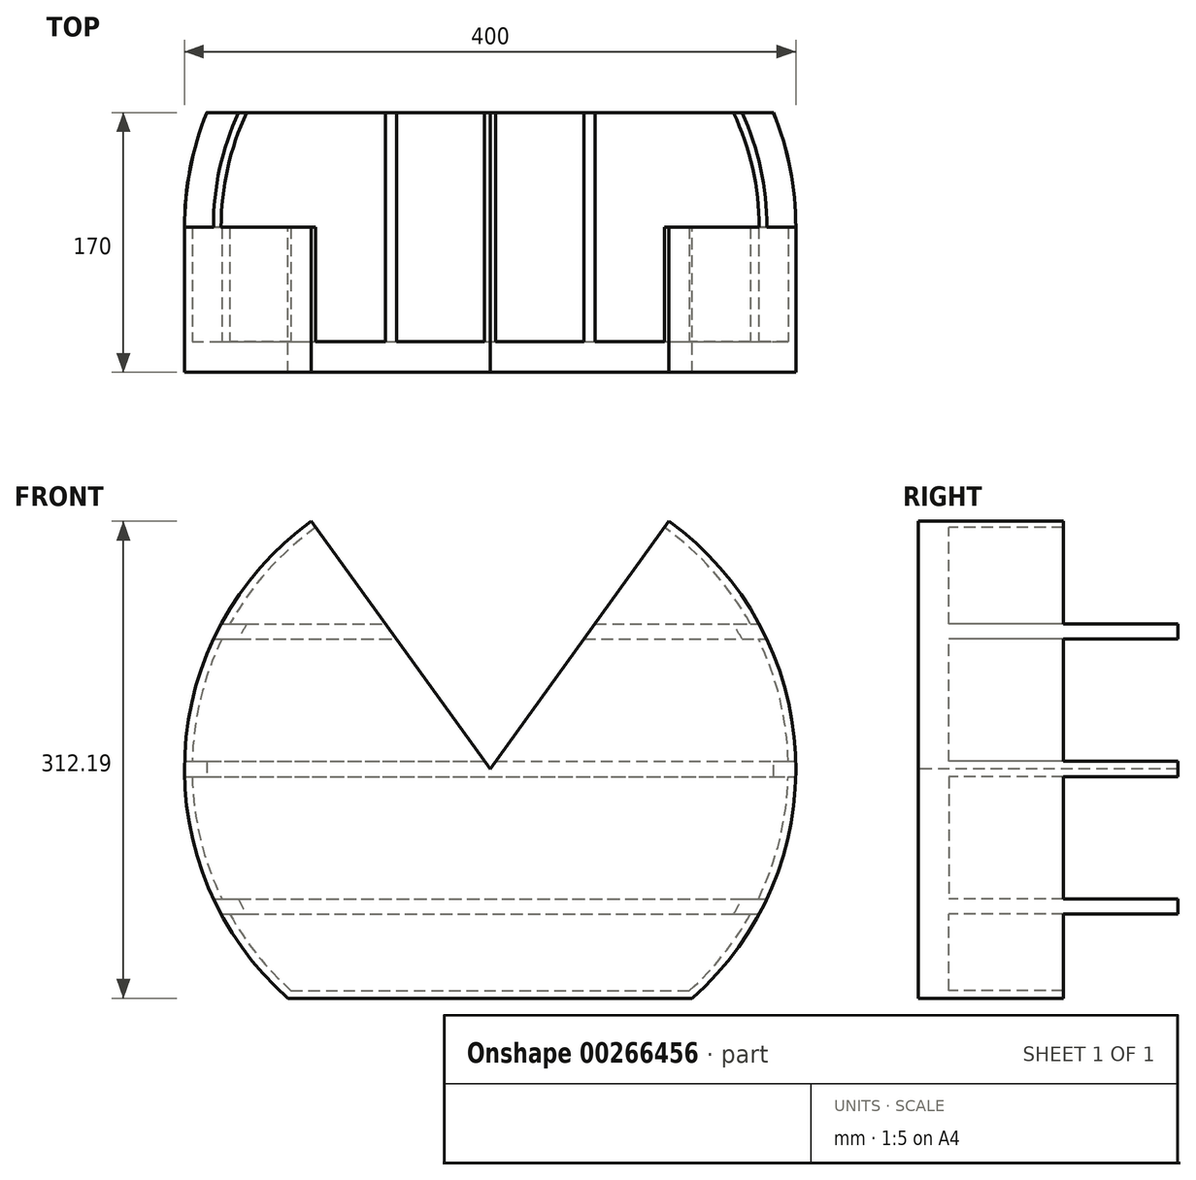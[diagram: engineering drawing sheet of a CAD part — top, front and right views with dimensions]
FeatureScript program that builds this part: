
annotation { "Feature Type Name" : "Feature", "Feature Type Description" : "" }
export const myFeature = defineFeature(function(context is Context, id is Id, definition is map)
    precondition{}
    {
        {
            var Q0;
            Q0=qCreatedBy(makeId("Front.planeOp"),FACE);
            var sketch = newSketch(context, id + "F0", { "sketchPlane" : qUnion([Q0])});
            skCircle(sketch, "E0", {"center": v(0, 0) * mm, "radius": 200 * mm});
            skSolve(sketch);
        }
        {
            var Q0;
            Q0=makeQuery(id+"F0.imprint","IMPRINT",FACE,{"disambiguationData":[TD([[makeQuery(id+"F0.imprint","IMPRINT",EDGE,{"derivedFrom":sQuery(id+"F0.wireOp",EDGE,"E0")}),1.0]])]});
            extrude(context, id + "F1", {"entities" : qUnion([Q0]), "depth" : 20 * mm});
        }
        {
            var Q0;
            Q0=makeQuery(id+"F1.opExtrude","CAP_FACE",FACE,{"disambiguationData":[OSD([sQuery(id+"F0.wireOp",EDGE,"E0")])],"isStart":true});
            var sketch = newSketch(context, id + "F2", { "sketchPlane" : qUnion([Q0])});
            skLineSegment(sketch, "E1.bottom", {"start": v(225, 5) * mm, "end": v(-225, 5) * mm});
            skLineSegment(sketch, "E1.top", {"start": v(225, -5) * mm, "end": v(-225, -5) * mm});
            skLineSegment(sketch, "E1.left", {"start": v(225, 5) * mm, "end": v(225, -5) * mm});
            skLineSegment(sketch, "E1.right", {"start": v(-225, 5) * mm, "end": v(-225, -5) * mm});
            skPoint(sketch, "E1.middle", {"position": v(0, 0) * mm});
            skLineSegment(sketch, "E2", {"start": v(0, 0) * mm, "end": v(0, 90) * mm, "construction": true});
            skPoint(sketch, "E2.endSnap0", {"position": v(0, 5) * mm});
            skLineSegment(sketch, "E3.bottom", {"start": v(224.66, 95) * mm, "end": v(-224.66, 95) * mm});
            skLineSegment(sketch, "E3.top", {"start": v(224.66, 85) * mm, "end": v(-224.66, 85) * mm});
            skLineSegment(sketch, "E3.left", {"start": v(224.66, 95) * mm, "end": v(224.66, 85) * mm});
            skLineSegment(sketch, "E3.right", {"start": v(-224.66, 95) * mm, "end": v(-224.66, 85) * mm});
            skPoint(sketch, "E3.middle", {"position": v(0, 90) * mm});
            skLineSegment(sketch, "E4", {"start": v(0, 0) * mm, "end": v(20.21, 0) * mm, "construction": true});
            skLineSegment(sketch, "E5.MirrorCS", {"start": v(224.66, -95) * mm, "end": v(224.66, -85) * mm});
            skLineSegment(sketch, "E6.MirrorCS", {"start": v(-224.66, -95) * mm, "end": v(-224.66, -85) * mm});
            skPoint(sketch, "E7.MirrorP", {"position": v(0, -90) * mm});
            skLineSegment(sketch, "E8.MirrorCS", {"start": v(224.66, -95) * mm, "end": v(-224.66, -95) * mm});
            skLineSegment(sketch, "E9.MirrorCS", {"start": v(224.66, -85) * mm, "end": v(-224.66, -85) * mm});
            skSolve(sketch);
        }
        {
            var Q0;
            {var subQ0=sQuery(id+"F2.wireOp",EDGE,"E3.bottom");var subQ1=makeQuery(id+"F1.opExtrude","CAP_EDGE",EDGE,{"disambiguationData":[OSD([sQuery(id+"F0.wireOp",EDGE,"E0")])],"isStart":true});var subQ2=makeQuery(id+"F2.imprint","INTERSECT",VERTEX,{"disambiguationData":[OD(0.0)],"derivedFrom":[subQ1,subQ0]});Q0=makeQuery(id+"F2.imprint","IMPRINT",FACE,{"disambiguationData":[TD([[makeQuery(id+"F2.imprint","IMPRINT",EDGE,{"disambiguationData":[TD([[subQ2,-1.0]])],"derivedFrom":subQ0}),1.0]])]});}
            var Q1;
            {var subQ0=sQuery(id+"F2.wireOp",EDGE,"E1.bottom");var subQ1=makeQuery(id+"F1.opExtrude","CAP_EDGE",EDGE,{"disambiguationData":[OSD([sQuery(id+"F0.wireOp",EDGE,"E0")])],"isStart":true});var subQ2=makeQuery(id+"F2.imprint","INTERSECT",VERTEX,{"disambiguationData":[OD(0.0)],"derivedFrom":[subQ1,subQ0]});Q1=makeQuery(id+"F2.imprint","IMPRINT",FACE,{"disambiguationData":[TD([[makeQuery(id+"F2.imprint","IMPRINT",EDGE,{"disambiguationData":[TD([[subQ2,-1.0]])],"derivedFrom":subQ0}),1.0]])]});}
            var Q2;
            {var subQ0=sQuery(id+"F2.wireOp",EDGE,"E8.MirrorCS");var subQ1=makeQuery(id+"F1.opExtrude","CAP_EDGE",EDGE,{"disambiguationData":[OSD([sQuery(id+"F0.wireOp",EDGE,"E0")])],"isStart":true});var subQ2=makeQuery(id+"F2.imprint","INTERSECT",VERTEX,{"disambiguationData":[OD(0.0)],"derivedFrom":[subQ1,subQ0]});Q2=makeQuery(id+"F2.imprint","IMPRINT",FACE,{"disambiguationData":[TD([[makeQuery(id+"F2.imprint","IMPRINT",EDGE,{"disambiguationData":[TD([[subQ2,-1.0]])],"derivedFrom":subQ0}),-1.0]])]});}
            extrude(context, id + "F3", {"entities" : qUnion([Q0, Q1, Q2]), "operationType" : NewBodyOperationType.ADD, "depth" : 150 * mm});
        }
        {
            var Q0;
            {var subQ1=sQuery(id+"F0.wireOp",EDGE,"E0");var subQ4=sQuery(id+"F2.wireOp",EDGE,"E3.bottom");Q0=makeQuery(id+"F3.boolean.opBoolean","SPLIT",FACE,{"disambiguationData":[TD([makeQuery(id+"F3.opExtrude","SWEPT_FACE",FACE,{"disambiguationData":[OSD([subQ4])]})])],"derivedFrom":makeQuery(id+"F1.opExtrude","CAP_FACE",FACE,{"disambiguationData":[OSD([subQ1])],"isStart":true})});}
            var sketch = newSketch(context, id + "F4", { "sketchPlane" : qUnion([Q0])});
            skCircle(sketch, "E10", {"center": v(0, 0) * mm, "radius": 200 * mm});
            skCircle(sketch, "E11", {"center": v(0, 0) * mm, "radius": 195 * mm});
            skSolve(sketch);
        }
        {
            var Q0;
            Q0 = qSketchRegion(id + "F4", true);
            extrude(context, id + "F5", {"entities" : qUnion([Q0]), "operationType" : NewBodyOperationType.ADD, "depth" : 75 * mm});
        }
        {
            var Q0;
            {var subQ0=sQuery(id+"F2.wireOp",EDGE,"E8.MirrorCS");var subQ1=sQuery(id+"F0.wireOp",EDGE,"E0");var subQ2=makeQuery(id+"F1.opExtrude","CAP_EDGE",EDGE,{"disambiguationData":[OSD([subQ1])],"isStart":true});var subQ4=sQuery(id+"F2.wireOp",EDGE,"E3.bottom");var subQ5=sQuery(id+"F2.wireOp",EDGE,"E3.top");var subQ6=sQuery(id+"F4.wireOp",EDGE,"E10");var subQ7=sQuery(id+"F2.wireOp",EDGE,"E1.bottom");var subQ9=sQuery(id+"F4.wireOp",EDGE,"E11");Q0=makeQuery(id+"F5.boolean.opBoolean","SPLIT",FACE,{"disambiguationData":[TD([makeQuery(id+"F1.opExtrude","SWEPT_FACE",FACE,{"disambiguationData":[OSD([subQ1])]}),makeQuery(id+"F3.opExtrude","SWEPT_FACE",FACE,{"disambiguationData":[OSD([subQ7])]}),makeQuery(id+"F3.opExtrude","SWEPT_FACE",FACE,{"disambiguationData":[OSD([subQ5])]}),makeQuery(id+"F3.opExtrude","SWEPT_FACE",FACE,{"disambiguationData":[OSD([subQ1]),TDD([makeQuery(id+"F2.imprint","IMPRINT",EDGE,{"disambiguationData":[TD([[makeQuery(id+"F2.imprint","INTERSECT",VERTEX,{"disambiguationData":[OD(0.0)],"derivedFrom":[subQ2,subQ7]}),-1.0]])],"derivedFrom":subQ2})])]}),makeQuery(id+"F3.opExtrude","SWEPT_FACE",FACE,{"disambiguationData":[OSD([subQ1]),TDD([makeQuery(id+"F2.imprint","IMPRINT",EDGE,{"disambiguationData":[TD([[makeQuery(id+"F2.imprint","INTERSECT",VERTEX,{"disambiguationData":[OD(1.0)],"derivedFrom":[subQ2,subQ7]}),1.0]])],"derivedFrom":subQ2})])]}),makeQuery(id+"F3.opExtrude","SWEPT_FACE",FACE,{"disambiguationData":[OSD([subQ1]),TDD([makeQuery(id+"F2.imprint","IMPRINT",EDGE,{"disambiguationData":[TD([[makeQuery(id+"F2.imprint","INTERSECT",VERTEX,{"disambiguationData":[OD(0.0)],"derivedFrom":[subQ2,subQ4]}),-1.0]])],"derivedFrom":subQ2})])]}),makeQuery(id+"F3.opExtrude","SWEPT_FACE",FACE,{"disambiguationData":[OSD([subQ1]),TDD([makeQuery(id+"F2.imprint","IMPRINT",EDGE,{"disambiguationData":[TD([[makeQuery(id+"F2.imprint","INTERSECT",VERTEX,{"disambiguationData":[OD(1.0)],"derivedFrom":[subQ2,subQ4]}),1.0]])],"derivedFrom":subQ2})])]}),makeQuery(id+"F3.opExtrude","SWEPT_FACE",FACE,{"disambiguationData":[OSD([subQ1]),TDD([makeQuery(id+"F2.imprint","IMPRINT",EDGE,{"disambiguationData":[TD([[makeQuery(id+"F2.imprint","INTERSECT",VERTEX,{"disambiguationData":[OD(0.0)],"derivedFrom":[subQ2,subQ0]}),1.0]])],"derivedFrom":subQ2})])]}),makeQuery(id+"F3.opExtrude","SWEPT_FACE",FACE,{"disambiguationData":[OSD([subQ1]),TDD([makeQuery(id+"F2.imprint","IMPRINT",EDGE,{"disambiguationData":[TD([[makeQuery(id+"F2.imprint","INTERSECT",VERTEX,{"disambiguationData":[OD(1.0)],"derivedFrom":[subQ2,subQ0]}),-1.0]])],"derivedFrom":subQ2})])]}),makeQuery(id+"F5.opExtrude","SWEPT_FACE",FACE,{"disambiguationData":[OSD([subQ6])]}),makeQuery(id+"F5.opExtrude","SWEPT_FACE",FACE,{"disambiguationData":[OSD([subQ9])]})]),OD(1.0)],"derivedFrom":makeQuery(id+"F5.opExtrude","CAP_FACE",FACE,{"disambiguationData":[OSD([subQ6,subQ9])],"isStart":false})});}
            var sketch = newSketch(context, id + "F6", { "sketchPlane" : qUnion([Q0])});
            skLineSegment(sketch, "E12", {"start": v(0, 0) * mm, "end": v(0, 506.05) * mm, "construction": true});
            skArc(sketch, "E13", {"start": v(0, -200) * mm, "mid": v(200, 0) * mm, "end": v(0, 200) * mm});
            skLineSegment(sketch, "E14", {"start": v(0, 200) * mm, "end": v(233.25, 200) * mm});
            skLineSegment(sketch, "E15", {"start": v(233.25, 200) * mm, "end": v(233.25, 0) * mm});
            skLineSegment(sketch, "E16", {"start": v(233.25, -200) * mm, "end": v(0, -200) * mm});
            skLineSegment(sketch, "E17", {"start": v(233.25, 0) * mm, "end": v(233.25, -200) * mm});
            skSolve(sketch);
        }
        {
            var Q0;
            Q0=makeQuery(id+"F6.imprint","IMPRINT",FACE,{"disambiguationData":[TD([[makeQuery(id+"F6.imprint","IMPRINT",EDGE,{"derivedFrom":sQuery(id+"F6.wireOp",EDGE,"E13")}),-1.0]])]});
            var Q1;
            Q1=sQuery(id+"F6.wireOp",EDGE,"E12");
            revolve(context, id + "F7", {"operationType" : NewBodyOperationType.REMOVE, "entities" : qUnion([Q0]), "axis" : qUnion([Q1]), "revolveType" : RevolveType.ONE_DIRECTION, "oppositeDirection" : true, "angle" : 180 * degree});
        }
        {
            var Q0;
            Q0=makeQuery(id+"F1.opExtrude","CAP_FACE",FACE,{"disambiguationData":[OSD([sQuery(id+"F0.wireOp",EDGE,"E0")])],"isStart":false});
            var sketch = newSketch(context, id + "F8", { "sketchPlane" : qUnion([Q0])});
            skLineSegment(sketch, "E18", {"start": v(0, 0) * mm, "end": v(0, 200) * mm, "construction": true});
            skArc(sketch, "E19", {"start": v(117.03, 162.19) * mm, "mid": v(61.5, 190.31) * mm, "end": v(0, 200) * mm});
            skPoint(sketch, "E20.MirrorCS.end.orphan", {"position": v(-146.92, 135.7) * mm});
            skLineSegment(sketch, "E21", {"start": v(0, 0) * mm, "end": v(117.03, 162.19) * mm});
            skPoint(sketch, "E22.orphan", {"position": v(146.92, 135.7) * mm});
            skArc(sketch, "E23.MirrorCS", {"start": v(-117.03, 162.19) * mm, "mid": v(-61.5, 190.31) * mm, "end": v(0, 200) * mm});
            skLineSegment(sketch, "E24.MirrorCS", {"start": v(0, 0) * mm, "end": v(-117.03, 162.19) * mm});
            skSolve(sketch);
        }
        {
            var Q0;
            Q0 = qSketchRegion(id + "F8", true);
            extrude(context, id + "F9", {"entities" : qUnion([Q0]), "operationType" : NewBodyOperationType.REMOVE, "endBound" : BoundingType.THROUGH_ALL, "oppositeDirection" : true, "depth" : 25 * mm});
        }
        {
            var Q0;
            Q0=makeQuery(id+"F1.opExtrude","CAP_FACE",FACE,{"disambiguationData":[OSD([sQuery(id+"F0.wireOp",EDGE,"E0")])],"isStart":false});
            var sketch = newSketch(context, id + "F10", { "sketchPlane" : qUnion([Q0])});
            skLineSegment(sketch, "E25", {"start": v(0, -200) * mm, "end": v(0, -150) * mm, "construction": true});
            skLineSegment(sketch, "E26.bottom", {"start": v(171.92, -150) * mm, "end": v(-171.92, -150) * mm});
            skLineSegment(sketch, "E26.top", {"start": v(171.92, -200) * mm, "end": v(-171.92, -200) * mm});
            skLineSegment(sketch, "E26.left", {"start": v(171.92, -150) * mm, "end": v(171.92, -200) * mm});
            skLineSegment(sketch, "E26.right", {"start": v(-171.92, -150) * mm, "end": v(-171.92, -200) * mm});
            skPoint(sketch, "E26.middle", {"position": v(0, -175) * mm});
            skSolve(sketch);
        }
        {
            var Q0;
            Q0 = qSketchRegion(id + "F10", true);
            extrude(context, id + "F11", {"entities" : qUnion([Q0]), "operationType" : NewBodyOperationType.REMOVE, "endBound" : BoundingType.THROUGH_ALL, "oppositeDirection" : true, "depth" : 25 * mm});
        }
        {
            var Q0;
            Q0=makeQuery(id+"F1.opExtrude","CAP_FACE",FACE,{"disambiguationData":[OSD([sQuery(id+"F0.wireOp",EDGE,"E0")])],"isStart":false});
            var sketch = newSketch(context, id + "F12", { "sketchPlane" : qUnion([Q0])});
            skArc(sketch, "E27", {"start": v(132.29, -150) * mm, "mid": v(135.04, -147.53) * mm, "end": v(137.75, -145) * mm});
            skLineSegment(sketch, "E28", {"start": v(-132.29, -150) * mm, "end": v(132.29, -150) * mm});
            skPoint(sketch, "E29.endSnap0", {"position": v(0, -150) * mm});
            skLineSegment(sketch, "E30", {"start": v(0, -145) * mm, "end": v(137.75, -145) * mm});
            skLineSegment(sketch, "E31", {"start": v(0, -145) * mm, "end": v(-137.75, -145) * mm});
            skPoint(sketch, "E29.start.orphan", {"position": v(0, -150) * mm});
            skArc(sketch, "E32.trimOffspring", {"start": v(-137.75, -145) * mm, "mid": v(-135.04, -147.53) * mm, "end": v(-132.29, -150) * mm});
            skSolve(sketch);
        }
        {
            var Q0;
            Q0 = qSketchRegion(id + "F12", true);
            extrude(context, id + "F13", {"entities" : qUnion([Q0]), "operationType" : NewBodyOperationType.ADD, "oppositeDirection" : true, "depth" : 95 * mm});
        }
    });
